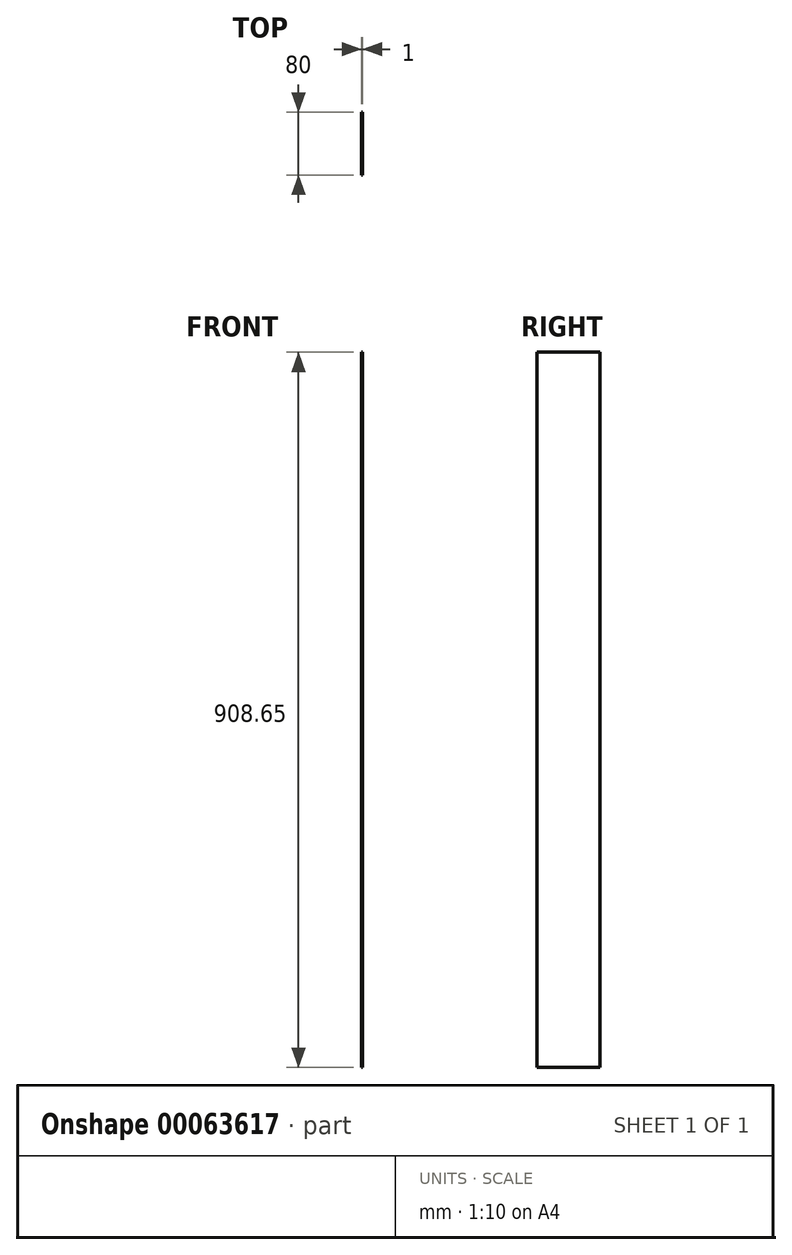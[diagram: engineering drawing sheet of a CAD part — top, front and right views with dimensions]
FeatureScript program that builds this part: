
annotation { "Feature Type Name" : "Feature", "Feature Type Description" : "" }
export const myFeature = defineFeature(function(context is Context, id is Id, definition is map)
    precondition{}
    {
        {
            var Q0;
            Q0=qCreatedBy(makeId("Right.planeOp"),FACE);
            var sketch = newSketch(context, id + "F0", { "sketchPlane" : qUnion([Q0])});
            skLineSegment(sketch, "E0.bottom", {"start": v(0, 0) * mm, "end": v(-80, 0) * mm});
            skLineSegment(sketch, "E0.top", {"start": v(0, -908.65) * mm, "end": v(-80, -908.65) * mm});
            skLineSegment(sketch, "E0.left", {"start": v(0, 0) * mm, "end": v(0, -908.65) * mm});
            skLineSegment(sketch, "E0.right", {"start": v(-80, 0) * mm, "end": v(-80, -908.65) * mm});
            skSolve(sketch);
        }
        {
            var Q0;
            Q0=makeQuery(id+"F0.imprint","IMPRINT",FACE,{"disambiguationData":[TD([[makeQuery(id+"F0.imprint","IMPRINT",EDGE,{"derivedFrom":sQuery(id+"F0.wireOp",EDGE,"E0.bottom")}),1.0]])]});
            extrude(context, id + "F1", {"entities" : qUnion([Q0]), "depth" : 1 * mm});
        }
    });
